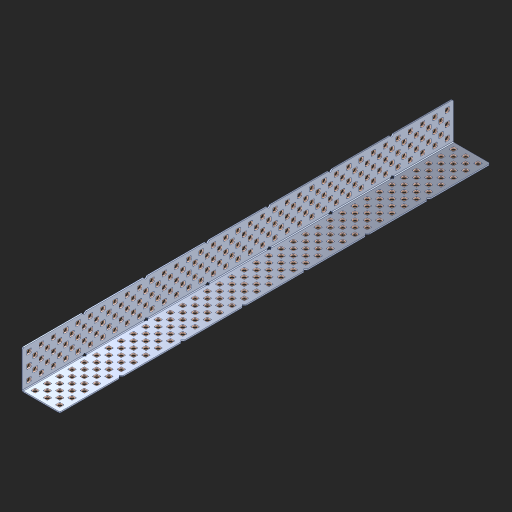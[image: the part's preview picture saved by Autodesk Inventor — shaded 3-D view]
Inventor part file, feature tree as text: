
AUTODESK INVENTOR PART (.ipt)
format: ipt  version: 2023 (Build 270158000, 158)  size: 3,318,784 bytes
history: native  units: in
note: dims shown in document units (in); Inventor stores cm internally (conversion verified against a paired STEP export)
features: other x388, extrude x344, sheet_metal_op x8, sketch x7, pattern_linear x3, mirror x1, chamfer x1
ambient origin geometry x8: Origin, YZ Plane, XZ Plane, XY Plane, X Axis, Y Axis, Z Axis, Center Point
bodies: Solid1 (feature_tree), Body (feature_tree)
feature tree (752):
  other  "Table"
  other  "Steel Angle 3x3x35"
  other  "Steel Angle 3x3x34"
  other  "Steel Angle 3x3x33"
  other  "Steel Angle 3x3x32"
  other  "Steel Angle 3x3x31"
  other  "Steel Angle 3x3x30"
  other  "Steel Angle 3x3x29"
  other  "Steel Angle 3x3x28"
  other  "Steel Angle 3x3x27"
  other  "Steel Angle 3x3x26"
  other  "Steel Angle 3x3x25"
  other  "Steel Angle 3x3x24"
  other  "Steel Angle 3x3x23"
  other  "Steel Angle 3x3x22"
  other  "Steel Angle 3x3x21"
  other  "Steel Angle 3x3x20"
  other  "Steel Angle 3x3x19"
  other  "Steel Angle 3x3x18"
  other  "Steel Angle 3x3x17"
  other  "Steel Angle 3x3x16"
  other  "Steel Angle 3x3x15"
  other  "Steel Angle 3x3x14"
  other  "Steel Angle 3x3x13"
  other  "Steel Angle 3x3x12"
  other  "Steel Angle 3x3x11"
  other  "Steel Angle 3x3x10"
  other  "Steel Angle 3x3x9"
  other  "Steel Angle 3x3x8"
  other  "Steel Angle 3x3x7"
  other  "Steel Angle 3x3x6"
  other  "Steel Angle 3x3x5"
  other  "Steel Angle 3x3x4"
  other  "Steel Angle 3x3x3"
  other  "Steel Angle 3x3x2"
  other  "Steel Angle 3x3x1"
  sheet_metal_op  "Flanges"
  sheet_metal_op  "Body Pattern"
  pattern_linear  "Center Double"  Spacing1=1.5in  [1 undecoded]
  pattern_linear  "Center Pattern"  Spacing1=0.1875in  [1 undecoded]
  other  "Arc Length"
  pattern_linear  "Notch Pattern"  Spacing1=0.0469in  [1 undecoded]
  other  "Diagonal Plane"
  mirror  "Everything Mirrored"
  chamfer  "End Chamfer"
  sketch  "Sketch1"  dims[d0=1.5in]
  other  "Plate1"
  sketch  "Sketch2"  dims[d1=17.5in]
  other  "Plate2"
  sheet_metal_op  "Bend1"
  sheet_metal_op  "Corner1"
  sketch  "Sketch8"  dims[d2=0.0469in]
  sketch  "Sketch9"  dims[d3=0.0469in]
  other  "Srf91"
  sheet_metal_op  "Body Pattern Sketch"
  other  "Srf92"
  sketch  "Sketch13"  dims[d4=0.0234in]
  sketch  "Sketch15"  dims[d5=0.0938in]
  sketch  "Sketch16"  dims[d6=0.0469in d7=1.5in d8=90.0deg d9=0.0312in d10=0.1875in d11=0.0469in d12=0.0469in d49=0.182in d50=0.02in d52=0.25in d53=0.0469in d54=0.0in d55=0.172in d56=1.0in d57=0.0in d85=0.1473in d86=0.1659in d89=0.0469in d90=0.0in d91=0.04in d92=0.0491in d95=2.5in d96=0.04in d97=0.25in d98=45.0deg d106=0.182in d107=0.02in d110=0.0469in d111=0.0in d112=0.172in d113=0.5in d114=0.0in d117=0.5in d126=0.0491in d127=0.1227in d128=0.08in d129=0.04in d130=2.5in d131=0.25in d132=13.7795in d134=0.5in d135=1.1811in d137=0.5in d140=0.5in d141=1.0in d142=0.3937in d144=0.5in d145=0.071in d146=0.7874in d148=0.5in]
  other  "Srf786"
  other  "Srf856"
  other  "Srf889"
  other  "Srf890"
  other  "Srf891"
  other  "Srf1275"
  other  "Srf1276"
  other  "Srf1278"
  other  "Srf1277"
  other  "Srf1285"
  other  "Srf1286"
  other  "Srf1287"
  other  "Srf1445"
  other  "Srf1446"
  other  "Srf1447"
  other  "Srf1448"
  other  "Srf1449"
  other  "Srf1537"
  other  "Srf1538"
  other  "Srf1539"
  other  "Srf1540"
  other  "Srf1541"
  other  "Srf1807"
  other  "Srf1808"
  other  "Srf1809"
  other  "Srf1810"
  other  "Srf1811"
  other  "Srf1812"
  other  "Srf1813"
  other  "Srf1814"
  other  "Srf1815"
  other  "Srf1816"
  other  "Srf1817"
  other  "Srf1818"
  other  "Srf1819"
  other  "Srf1820"
  other  "Srf1821"
  other  "Srf1822"
  other  "Srf1823"
  other  "Srf1824"
  other  "Srf1825"
  other  "Srf1826"
  other  "Srf1827"
  other  "Srf1828"
  other  "Srf1829"
  other  "Srf1830"
  other  "Srf1831"
  other  "Srf1959"
  other  "Srf1960"
  other  "Srf1961"
  other  "Srf1962"
  other  "Srf1963"
  other  "Srf1964"
  other  "Srf1965"
  other  "Srf1966"
  other  "Srf1967"
  other  "Srf1968"
  other  "Srf1969"
  other  "Srf1970"
  other  "Srf1971"
  other  "Srf1972"
  other  "Srf1973"
  other  "Srf1974"
  other  "Srf1975"
  other  "Srf1976"
  other  "Srf1977"
  other  "Srf1978"
  other  "Srf1979"
  other  "Srf1980"
  other  "Srf1981"
  other  "Srf1982"
  other  "Srf1983"
  other  "Srf2009"
  other  "Srf2010"
  other  "Srf2011"
  other  "Srf2012"
  other  "Srf2013"
  other  "Srf2014"
  other  "Srf2015"
  other  "Srf2016"
  other  "Srf2017"
  other  "Srf2018"
  other  "Srf2019"
  other  "Srf2020"
  other  "Srf2021"
  other  "Srf2022"
  other  "Srf2023"
  other  "Srf2024"
  other  "Srf2025"
  other  "Srf2026"
  other  "Srf2027"
  other  "Srf2028"
  other  "Srf2029"
  other  "Srf2030"
  other  "Srf2031"
  other  "Srf2032"
  other  "Srf2033"
  other  "Srf2034"
  other  "Srf2035"
  other  "Srf2036"
  other  "Srf2037"
  other  "Srf2038"
  other  "Srf2039"
  other  "Srf2040"
  other  "Srf2041"
  other  "Srf2042"
  other  "Srf2043"
  other  "Srf2044"
  other  "Srf2045"
  other  "Srf2046"
  other  "Srf2047"
  other  "Srf2048"
  other  "Srf2049"
  other  "Srf2050"
  other  "Srf2051"
  other  "Srf2052"
  other  "Srf2053"
  other  "Srf2054"
  other  "Srf2055"
  other  "Srf2056"
  other  "Srf2057"
  other  "Srf2058"
  other  "Srf2059"
  other  "Srf2060"
  other  "Srf2061"
  other  "Srf2062"
  other  "Srf2063"
  other  "Srf2064"
  other  "Srf2065"
  other  "Srf2066"
  other  "Srf2067"
  other  "Srf2068"
  other  "Srf2069"
  other  "Srf2070"
  other  "Srf2071"
  other  "Srf2072"
  other  "Srf2073"
  other  "Srf2074"
  other  "Srf2075"
  other  "Srf2076"
  other  "Srf2077"
  other  "Srf2078"
  other  "Srf2079"
  other  "Srf2080"
  other  "Srf2081"
  other  "Srf2082"
  other  "Srf2083"
  other  "Srf2084"
  other  "Srf2085"
  other  "Srf2086"
  other  "Srf2087"
  other  "Srf2088"
  other  "Srf2089"
  other  "Srf2090"
  other  "Srf2091"
  other  "Srf2092"
  other  "Srf2093"
  other  "Srf2094"
  other  "Srf2095"
  other  "Srf2096"
  other  "Srf2097"
  other  "Srf2098"
  other  "Srf2099"
  other  "Srf2100"
  other  "Srf2101"
  other  "Srf2102"
  other  "Srf2103"
  other  "Srf2104"
  other  "Srf2105"
  other  "Srf2106"
  other  "Srf2107"
  other  "Srf2108"
  other  "Srf2109"
  other  "Srf2110"
  other  "Srf2111"
  other  "Srf2112"
  other  "Srf2113"
  other  "Srf2114"
  other  "Srf2115"
  other  "Srf2116"
  other  "Srf2117"
  other  "Srf2118"
  other  "Srf2119"
  other  "Srf2120"
  other  "Srf2121"
  other  "Srf2122"
  other  "Srf2123"
  other  "Srf2124"
  other  "Srf2125"
  other  "Srf2126"
  other  "Srf2127"
  other  "Srf2128"
  other  "Srf2129"
  other  "Srf2130"
  other  "Srf2131"
  other  "Srf2132"
  other  "Srf2133"
  other  "Srf2134"
  other  "Srf2135"
  other  "Srf2136"
  other  "Srf2137"
  other  "Srf2138"
  other  "Srf2139"
  other  "Srf2140"
  other  "Srf2141"
  other  "Srf2142"
  other  "Srf2143"
  other  "Srf2144"
  other  "Srf2145"
  other  "Srf2146"
  other  "Srf2147"
  other  "Srf2148"
  other  "Srf2149"
  other  "Srf2150"
  other  "Srf2151"
  other  "Srf2152"
  other  "Srf2153"
  other  "Srf2154"
  other  "Srf2155"
  other  "Srf2156"
  other  "Srf2157"
  other  "Srf2158"
  other  "Srf2159"
  other  "Srf2160"
  other  "Srf2161"
  other  "Srf2162"
  other  "Srf2163"
  other  "Srf2164"
  other  "Srf2165"
  other  "Srf2166"
  other  "Srf2167"
  other  "Srf2168"
  other  "Srf2169"
  other  "Srf2170"
  other  "Srf2171"
  other  "Srf2172"
  other  "Srf2173"
  other  "Srf2174"
  other  "Srf2175"
  other  "Srf2176"
  other  "Srf2177"
  other  "Srf2178"
  other  "Srf2179"
  other  "Srf2180"
  other  "Srf2181"
  other  "Srf2182"
  other  "Srf2183"
  other  "Srf2184"
  other  "Srf2185"
  other  "Srf2186"
  other  "Srf2187"
  other  "Srf2188"
  other  "Srf2189"
  other  "Srf2190"
  other  "Srf2191"
  other  "Srf2192"
  other  "Srf2193"
  other  "Srf2194"
  other  "Srf2195"
  other  "Srf2196"
  other  "Srf2197"
  other  "Srf2198"
  other  "Srf2199"
  other  "Srf2200"
  other  "Srf2201"
  other  "Srf2202"
  other  "Srf2203"
  other  "Srf2204"
  other  "Srf2205"
  other  "Srf2206"
  other  "Srf2207"
  other  "Srf2208"
  other  "Srf2209"
  other  "Srf2210"
  other  "Srf2211"
  other  "Srf2212"
  other  "Srf2213"
  other  "Srf2214"
  other  "Srf2215"
  other  "Srf2216"
  other  "Srf2217"
  other  "Srf2218"
  other  "Srf2219"
  other  "Srf2220"
  other  "Srf2221"
  other  "Srf2222"
  other  "Srf2223"
  other  "Srf2224"
  other  "Srf2225"
  other  "Srf2226"
  other  "Srf2227"
  other  "Srf2228"
  other  "Srf2229"
  other  "Srf2230"
  other  "Srf2231"
  other  "Srf2232"
  other  "Srf2233"
  other  "Srf2234"
  other  "Srf2235"
  other  "Srf2236"
  other  "Srf2237"
  other  "Srf2238"
  other  "Srf2239"
  other  "Srf2240"
  other  "Srf2241"
  other  "Srf2242"
  other  "Srf2243"
  other  "Srf2244"
  other  "Srf2245"
  other  "Srf2246"
  other  "Srf2247"
  other  "Srf2248"
  other  "Srf2249"
  other  "Srf2250"
  other  "Srf2251"
  other  "Srf2252"
  other  "Srf2253"
  other  "Srf2254"
  other  "Srf2255"
  other  "Srf2256"
  other  "Srf2257"
  other  "Srf2258"
  other  "Srf2259"
  other  "Srf2260"
  other  "Srf2261"
  other  "Srf2262"
  other  "Srf2263"
  other  "Srf2264"
  other  "Srf2265"
  other  "Srf2266"
  other  "Srf2267"
  other  "Srf2268"
  other  "Srf2269"
  other  "Srf2270"
  other  "Srf2271"
  other  "Srf2272"
  other  "Srf2273"
  other  "Srf2274"
  other  "Srf2275"
  other  "Srf2276"
  other  "Srf2277"
  other  "Srf2278"
  other  "Srf2279"
  other  "Srf2280"
  sheet_metal_op  "Body Stamp"
  sheet_metal_op  "Body Circle"
  other  "Center Stamp"
  other  "Center Circle"
  sheet_metal_op  "Notch"
  extrude  "ExtrusionSrf92"  Depth=0.0469in
  extrude  "ExtrusionSrf856"  Depth=0.3937in
  extrude  "ExtrusionSrf889"  Depth=0.02in
  extrude  "ExtrusionSrf890"  Depth=0.25in
  extrude  "ExtrusionSrf891"  Depth=0.0469in
  extrude  "ExtrusionSrf1275"  TaperAngle=0.0deg  [1 undecoded]
  extrude  "ExtrusionSrf1276"  Depth=0.3937in
  extrude  "ExtrusionSrf1277"  Depth=0.3937in TaperAngle=0.0deg
  extrude  "ExtrusionSrf1345"  Depth=0.3937in
  extrude  "ExtrusionSrf1346"  Depth=0.3937in
  extrude  "ExtrusionSrf1347"  Depth=0.0469in
  extrude  "ExtrusionSrf1348"  Depth=0.3937in TaperAngle=0.0deg
  extrude  "ExtrusionSrf1445"  Depth=0.3937in
  extrude  "ExtrusionSrf1446"  Depth=0.25in TaperAngle=45.0deg
  extrude  "ExtrusionSrf1447"  Depth=0.3937in
  extrude  "ExtrusionSrf1448"  Depth=0.02in
  extrude  "ExtrusionSrf1449"  Depth=0.0469in
  extrude  "ExtrusionSrf1537"  TaperAngle=0.0deg  [1 undecoded]
  extrude  "ExtrusionSrf1538"  Depth=0.3937in
  extrude  "ExtrusionSrf1539"  Depth=0.3937in TaperAngle=0.0deg
  extrude  "ExtrusionSrf1540"  Depth=0.3937in
  extrude  "ExtrusionSrf1541"  Depth=0.3937in
  extrude  "ExtrusionSrf1807"  Depth=0.3937in
  extrude  "ExtrusionSrf1808"  Depth=0.3937in
  extrude  "ExtrusionSrf1809"  Depth=0.3937in
  extrude  "ExtrusionSrf1810"  Depth=0.3937in
  extrude  "ExtrusionSrf1811"  Depth=0.25in
  extrude  "ExtrusionSrf1812"  Depth=0.3937in
  extrude  "ExtrusionSrf1813"  Depth=0.3937in
  extrude  "ExtrusionSrf1814"  Depth=0.3937in
  extrude  "ExtrusionSrf1815"  Depth=0.3937in
  extrude  "ExtrusionSrf1816"  Depth=0.3937in
  extrude  "ExtrusionSrf1817"  Depth=0.3937in
  extrude  "ExtrusionSrf1818"  Depth=0.3937in
  extrude  "ExtrusionSrf1819"  [1 undecoded]
  extrude  "ExtrusionSrf1820"  [1 undecoded]
  extrude  "ExtrusionSrf1821"  [1 undecoded]
  extrude  "ExtrusionSrf1822"  [1 undecoded]
  extrude  "ExtrusionSrf1823"  [1 undecoded]
  extrude  "ExtrusionSrf1824"  [1 undecoded]
  extrude  "ExtrusionSrf1825"  [1 undecoded]
  extrude  "ExtrusionSrf1826"  [1 undecoded]
  extrude  "ExtrusionSrf1827"  [1 undecoded]
  extrude  "ExtrusionSrf1828"  [1 undecoded]
  extrude  "ExtrusionSrf1829"  [1 undecoded]
  extrude  "ExtrusionSrf1830"  [1 undecoded]
  extrude  "ExtrusionSrf1831"  [1 undecoded]
  extrude  "ExtrusionSrf1959"  [1 undecoded]
  extrude  "ExtrusionSrf1960"  [1 undecoded]
  extrude  "ExtrusionSrf1961"  [1 undecoded]
  extrude  "ExtrusionSrf1962"  [1 undecoded]
  extrude  "ExtrusionSrf1963"  [1 undecoded]
  extrude  "ExtrusionSrf1964"  [1 undecoded]
  extrude  "ExtrusionSrf1965"  [1 undecoded]
  extrude  "ExtrusionSrf1966"  [1 undecoded]
  extrude  "ExtrusionSrf1967"  [1 undecoded]
  extrude  "ExtrusionSrf1968"  [1 undecoded]
  extrude  "ExtrusionSrf1969"  [1 undecoded]
  extrude  "ExtrusionSrf1970"  [1 undecoded]
  extrude  "ExtrusionSrf1971"  [1 undecoded]
  extrude  "ExtrusionSrf1972"  [1 undecoded]
  extrude  "ExtrusionSrf1973"  [1 undecoded]
  extrude  "ExtrusionSrf1974"  [1 undecoded]
  extrude  "ExtrusionSrf1975"  [1 undecoded]
  extrude  "ExtrusionSrf1976"  [1 undecoded]
  extrude  "ExtrusionSrf1977"  [1 undecoded]
  extrude  "ExtrusionSrf1978"  [1 undecoded]
  extrude  "ExtrusionSrf1979"  [1 undecoded]
  extrude  "ExtrusionSrf1980"  [1 undecoded]
  extrude  "ExtrusionSrf1981"  [1 undecoded]
  extrude  "ExtrusionSrf1982"  [1 undecoded]
  extrude  "ExtrusionSrf1983"  [1 undecoded]
  extrude  "ExtrusionSrf2009"  [1 undecoded]
  extrude  "ExtrusionSrf2010"  [1 undecoded]
  extrude  "ExtrusionSrf2011"  [1 undecoded]
  extrude  "ExtrusionSrf2012"  [1 undecoded]
  extrude  "ExtrusionSrf2013"  [1 undecoded]
  extrude  "ExtrusionSrf2014"  [1 undecoded]
  extrude  "ExtrusionSrf2015"  [1 undecoded]
  extrude  "ExtrusionSrf2016"  [1 undecoded]
  extrude  "ExtrusionSrf2017"  [1 undecoded]
  extrude  "ExtrusionSrf2018"  [1 undecoded]
  extrude  "ExtrusionSrf2019"  [1 undecoded]
  extrude  "ExtrusionSrf2020"  [1 undecoded]
  extrude  "ExtrusionSrf2021"  [1 undecoded]
  extrude  "ExtrusionSrf2022"  [1 undecoded]
  extrude  "ExtrusionSrf2023"  [1 undecoded]
  extrude  "ExtrusionSrf2024"  [1 undecoded]
  extrude  "ExtrusionSrf2025"  [1 undecoded]
  extrude  "ExtrusionSrf2026"  [1 undecoded]
  extrude  "ExtrusionSrf2027"  [1 undecoded]
  extrude  "ExtrusionSrf2028"  [1 undecoded]
  extrude  "ExtrusionSrf2029"  [1 undecoded]
  extrude  "ExtrusionSrf2030"  [1 undecoded]
  extrude  "ExtrusionSrf2031"  [1 undecoded]
  extrude  "ExtrusionSrf2032"  [1 undecoded]
  extrude  "ExtrusionSrf2033"  [1 undecoded]
  extrude  "ExtrusionSrf2034"  [1 undecoded]
  extrude  "ExtrusionSrf2035"  [1 undecoded]
  extrude  "ExtrusionSrf2036"  [1 undecoded]
  extrude  "ExtrusionSrf2037"  [1 undecoded]
  extrude  "ExtrusionSrf2038"  [1 undecoded]
  extrude  "ExtrusionSrf2039"  [1 undecoded]
  extrude  "ExtrusionSrf2040"  [1 undecoded]
  extrude  "ExtrusionSrf2041"  [1 undecoded]
  extrude  "ExtrusionSrf2042"  [1 undecoded]
  extrude  "ExtrusionSrf2043"  [1 undecoded]
  extrude  "ExtrusionSrf2044"  [1 undecoded]
  extrude  "ExtrusionSrf2045"  [1 undecoded]
  extrude  "ExtrusionSrf2046"  [1 undecoded]
  extrude  "ExtrusionSrf2047"  [1 undecoded]
  extrude  "ExtrusionSrf2048"  [1 undecoded]
  extrude  "ExtrusionSrf2049"  [1 undecoded]
  extrude  "ExtrusionSrf2050"  [1 undecoded]
  extrude  "ExtrusionSrf2051"  [1 undecoded]
  extrude  "ExtrusionSrf2052"  [1 undecoded]
  extrude  "ExtrusionSrf2053"  [1 undecoded]
  extrude  "ExtrusionSrf2054"  [1 undecoded]
  extrude  "ExtrusionSrf2055"  [1 undecoded]
  extrude  "ExtrusionSrf2056"  [1 undecoded]
  extrude  "ExtrusionSrf2057"  [1 undecoded]
  extrude  "ExtrusionSrf2058"  [1 undecoded]
  extrude  "ExtrusionSrf2059"  [1 undecoded]
  extrude  "ExtrusionSrf2060"  [1 undecoded]
  extrude  "ExtrusionSrf2061"  [1 undecoded]
  extrude  "ExtrusionSrf2062"  [1 undecoded]
  extrude  "ExtrusionSrf2063"  [1 undecoded]
  extrude  "ExtrusionSrf2064"  [1 undecoded]
  extrude  "ExtrusionSrf2065"  [1 undecoded]
  extrude  "ExtrusionSrf2066"  [1 undecoded]
  extrude  "ExtrusionSrf2067"  [1 undecoded]
  extrude  "ExtrusionSrf2068"  [1 undecoded]
  extrude  "ExtrusionSrf2069"  [1 undecoded]
  extrude  "ExtrusionSrf2070"  [1 undecoded]
  extrude  "ExtrusionSrf2071"  [1 undecoded]
  extrude  "ExtrusionSrf2072"  [1 undecoded]
  extrude  "ExtrusionSrf2073"  [1 undecoded]
  extrude  "ExtrusionSrf2074"  [1 undecoded]
  extrude  "ExtrusionSrf2075"  [1 undecoded]
  extrude  "ExtrusionSrf2076"  [1 undecoded]
  extrude  "ExtrusionSrf2077"  [1 undecoded]
  extrude  "ExtrusionSrf2078"  [1 undecoded]
  extrude  "ExtrusionSrf2079"  [1 undecoded]
  extrude  "ExtrusionSrf2080"  [1 undecoded]
  extrude  "ExtrusionSrf2081"  [1 undecoded]
  extrude  "ExtrusionSrf2082"  [1 undecoded]
  extrude  "ExtrusionSrf2083"  [1 undecoded]
  extrude  "ExtrusionSrf2084"  [1 undecoded]
  extrude  "ExtrusionSrf2085"  [1 undecoded]
  extrude  "ExtrusionSrf2086"  [1 undecoded]
  extrude  "ExtrusionSrf2087"  [1 undecoded]
  extrude  "ExtrusionSrf2088"  [1 undecoded]
  extrude  "ExtrusionSrf2089"  [1 undecoded]
  extrude  "ExtrusionSrf2090"  [1 undecoded]
  extrude  "ExtrusionSrf2091"  [1 undecoded]
  extrude  "ExtrusionSrf2092"  [1 undecoded]
  extrude  "ExtrusionSrf2093"  [1 undecoded]
  extrude  "ExtrusionSrf2094"  [1 undecoded]
  extrude  "ExtrusionSrf2095"  [1 undecoded]
  extrude  "ExtrusionSrf2096"  [1 undecoded]
  extrude  "ExtrusionSrf2097"  [1 undecoded]
  extrude  "ExtrusionSrf2098"  [1 undecoded]
  extrude  "ExtrusionSrf2099"  [1 undecoded]
  extrude  "ExtrusionSrf2100"  [1 undecoded]
  extrude  "ExtrusionSrf2101"  [1 undecoded]
  extrude  "ExtrusionSrf2102"  [1 undecoded]
  extrude  "ExtrusionSrf2103"  [1 undecoded]
  extrude  "ExtrusionSrf2104"  [1 undecoded]
  extrude  "ExtrusionSrf2105"  [1 undecoded]
  extrude  "ExtrusionSrf2106"  [1 undecoded]
  extrude  "ExtrusionSrf2107"  [1 undecoded]
  extrude  "ExtrusionSrf2108"  [1 undecoded]
  extrude  "ExtrusionSrf2109"  [1 undecoded]
  extrude  "ExtrusionSrf2110"  [1 undecoded]
  extrude  "ExtrusionSrf2111"  [1 undecoded]
  extrude  "ExtrusionSrf2112"  [1 undecoded]
  extrude  "ExtrusionSrf2113"  [1 undecoded]
  extrude  "ExtrusionSrf2114"  [1 undecoded]
  extrude  "ExtrusionSrf2115"  [1 undecoded]
  extrude  "ExtrusionSrf2116"  [1 undecoded]
  extrude  "ExtrusionSrf2117"  [1 undecoded]
  extrude  "ExtrusionSrf2118"  [1 undecoded]
  extrude  "ExtrusionSrf2119"  [1 undecoded]
  extrude  "ExtrusionSrf2120"  [1 undecoded]
  extrude  "ExtrusionSrf2121"  [1 undecoded]
  extrude  "ExtrusionSrf2122"  [1 undecoded]
  extrude  "ExtrusionSrf2123"  [1 undecoded]
  extrude  "ExtrusionSrf2124"  [1 undecoded]
  extrude  "ExtrusionSrf2125"  [1 undecoded]
  extrude  "ExtrusionSrf2126"  [1 undecoded]
  extrude  "ExtrusionSrf2127"  [1 undecoded]
  extrude  "ExtrusionSrf2128"  [1 undecoded]
  extrude  "ExtrusionSrf2129"  [1 undecoded]
  extrude  "ExtrusionSrf2130"  [1 undecoded]
  extrude  "ExtrusionSrf2131"  [1 undecoded]
  extrude  "ExtrusionSrf2132"  [1 undecoded]
  extrude  "ExtrusionSrf2133"  [1 undecoded]
  extrude  "ExtrusionSrf2134"  [1 undecoded]
  extrude  "ExtrusionSrf2135"  [1 undecoded]
  extrude  "ExtrusionSrf2136"  [1 undecoded]
  extrude  "ExtrusionSrf2137"  [1 undecoded]
  extrude  "ExtrusionSrf2138"  [1 undecoded]
  extrude  "ExtrusionSrf2139"  [1 undecoded]
  extrude  "ExtrusionSrf2140"  [1 undecoded]
  extrude  "ExtrusionSrf2141"  [1 undecoded]
  extrude  "ExtrusionSrf2142"  [1 undecoded]
  extrude  "ExtrusionSrf2143"  [1 undecoded]
  extrude  "ExtrusionSrf2144"  [1 undecoded]
  extrude  "ExtrusionSrf2145"  [1 undecoded]
  extrude  "ExtrusionSrf2146"  [1 undecoded]
  extrude  "ExtrusionSrf2147"  [1 undecoded]
  extrude  "ExtrusionSrf2148"  [1 undecoded]
  extrude  "ExtrusionSrf2149"  [1 undecoded]
  extrude  "ExtrusionSrf2150"  [1 undecoded]
  extrude  "ExtrusionSrf2151"  [1 undecoded]
  extrude  "ExtrusionSrf2152"  [1 undecoded]
  extrude  "ExtrusionSrf2153"  [1 undecoded]
  extrude  "ExtrusionSrf2154"  [1 undecoded]
  extrude  "ExtrusionSrf2155"  [1 undecoded]
  extrude  "ExtrusionSrf2156"  [1 undecoded]
  extrude  "ExtrusionSrf2157"  [1 undecoded]
  extrude  "ExtrusionSrf2158"  [1 undecoded]
  extrude  "ExtrusionSrf2159"  [1 undecoded]
  extrude  "ExtrusionSrf2160"  [1 undecoded]
  extrude  "ExtrusionSrf2161"  [1 undecoded]
  extrude  "ExtrusionSrf2162"  [1 undecoded]
  extrude  "ExtrusionSrf2163"  [1 undecoded]
  extrude  "ExtrusionSrf2164"  [1 undecoded]
  extrude  "ExtrusionSrf2165"  [1 undecoded]
  extrude  "ExtrusionSrf2166"  [1 undecoded]
  extrude  "ExtrusionSrf2167"  [1 undecoded]
  extrude  "ExtrusionSrf2168"  [1 undecoded]
  extrude  "ExtrusionSrf2169"  [1 undecoded]
  extrude  "ExtrusionSrf2170"  [1 undecoded]
  extrude  "ExtrusionSrf2171"  [1 undecoded]
  extrude  "ExtrusionSrf2172"  [1 undecoded]
  extrude  "ExtrusionSrf2173"  [1 undecoded]
  extrude  "ExtrusionSrf2174"  [1 undecoded]
  extrude  "ExtrusionSrf2175"  [1 undecoded]
  extrude  "ExtrusionSrf2176"  [1 undecoded]
  extrude  "ExtrusionSrf2177"  [1 undecoded]
  extrude  "ExtrusionSrf2178"  [1 undecoded]
  extrude  "ExtrusionSrf2179"  [1 undecoded]
  extrude  "ExtrusionSrf2180"  [1 undecoded]
  extrude  "ExtrusionSrf2181"  [1 undecoded]
  extrude  "ExtrusionSrf2182"  [1 undecoded]
  extrude  "ExtrusionSrf2183"  [1 undecoded]
  extrude  "ExtrusionSrf2184"  [1 undecoded]
  extrude  "ExtrusionSrf2185"  [1 undecoded]
  extrude  "ExtrusionSrf2186"  [1 undecoded]
  extrude  "ExtrusionSrf2187"  [1 undecoded]
  extrude  "ExtrusionSrf2188"  [1 undecoded]
  extrude  "ExtrusionSrf2189"  [1 undecoded]
  extrude  "ExtrusionSrf2190"  [1 undecoded]
  extrude  "ExtrusionSrf2191"  [1 undecoded]
  extrude  "ExtrusionSrf2192"  [1 undecoded]
  extrude  "ExtrusionSrf2193"  [1 undecoded]
  extrude  "ExtrusionSrf2194"  [1 undecoded]
  extrude  "ExtrusionSrf2195"  [1 undecoded]
  extrude  "ExtrusionSrf2196"  [1 undecoded]
  extrude  "ExtrusionSrf2197"  [1 undecoded]
  extrude  "ExtrusionSrf2198"  [1 undecoded]
  extrude  "ExtrusionSrf2199"  [1 undecoded]
  extrude  "ExtrusionSrf2200"  [1 undecoded]
  extrude  "ExtrusionSrf2201"  [1 undecoded]
  extrude  "ExtrusionSrf2202"  [1 undecoded]
  extrude  "ExtrusionSrf2203"  [1 undecoded]
  extrude  "ExtrusionSrf2204"  [1 undecoded]
  extrude  "ExtrusionSrf2205"  [1 undecoded]
  extrude  "ExtrusionSrf2206"  [1 undecoded]
  extrude  "ExtrusionSrf2207"  [1 undecoded]
  extrude  "ExtrusionSrf2208"  [1 undecoded]
  extrude  "ExtrusionSrf2209"  [1 undecoded]
  extrude  "ExtrusionSrf2210"  [1 undecoded]
  extrude  "ExtrusionSrf2211"  [1 undecoded]
  extrude  "ExtrusionSrf2212"  [1 undecoded]
  extrude  "ExtrusionSrf2213"  [1 undecoded]
  extrude  "ExtrusionSrf2214"  [1 undecoded]
  extrude  "ExtrusionSrf2215"  [1 undecoded]
  extrude  "ExtrusionSrf2216"  [1 undecoded]
  extrude  "ExtrusionSrf2217"  [1 undecoded]
  extrude  "ExtrusionSrf2218"  [1 undecoded]
  extrude  "ExtrusionSrf2219"  [1 undecoded]
  extrude  "ExtrusionSrf2220"  [1 undecoded]
  extrude  "ExtrusionSrf2221"  [1 undecoded]
  extrude  "ExtrusionSrf2222"  [1 undecoded]
  extrude  "ExtrusionSrf2223"  [1 undecoded]
  extrude  "ExtrusionSrf2224"  [1 undecoded]
  extrude  "ExtrusionSrf2225"  [1 undecoded]
  extrude  "ExtrusionSrf2226"  [1 undecoded]
  extrude  "ExtrusionSrf2227"  [1 undecoded]
  extrude  "ExtrusionSrf2228"  [1 undecoded]
  extrude  "ExtrusionSrf2229"  [1 undecoded]
  extrude  "ExtrusionSrf2230"  [1 undecoded]
  extrude  "ExtrusionSrf2231"  [1 undecoded]
  extrude  "ExtrusionSrf2232"  [1 undecoded]
  extrude  "ExtrusionSrf2233"  [1 undecoded]
  extrude  "ExtrusionSrf2234"  [1 undecoded]
  extrude  "ExtrusionSrf2235"  [1 undecoded]
  extrude  "ExtrusionSrf2236"  [1 undecoded]
  extrude  "ExtrusionSrf2237"  [1 undecoded]
  extrude  "ExtrusionSrf2238"  [1 undecoded]
  extrude  "ExtrusionSrf2239"  [1 undecoded]
  extrude  "ExtrusionSrf2240"  [1 undecoded]
  extrude  "ExtrusionSrf2241"  [1 undecoded]
  extrude  "ExtrusionSrf2242"  [1 undecoded]
  extrude  "ExtrusionSrf2243"  [1 undecoded]
  extrude  "ExtrusionSrf2244"  [1 undecoded]
  extrude  "ExtrusionSrf2245"  [1 undecoded]
  extrude  "ExtrusionSrf2246"  [1 undecoded]
  extrude  "ExtrusionSrf2247"  [1 undecoded]
  extrude  "ExtrusionSrf2248"  [1 undecoded]
  extrude  "ExtrusionSrf2249"  [1 undecoded]
  extrude  "ExtrusionSrf2250"  [1 undecoded]
  extrude  "ExtrusionSrf2251"  [1 undecoded]
  extrude  "ExtrusionSrf2252"  [1 undecoded]
  extrude  "ExtrusionSrf2253"  [1 undecoded]
  extrude  "ExtrusionSrf2254"  [1 undecoded]
  extrude  "ExtrusionSrf2255"  [1 undecoded]
  extrude  "ExtrusionSrf2256"  [1 undecoded]
  extrude  "ExtrusionSrf2257"  [1 undecoded]
  extrude  "ExtrusionSrf2258"  [1 undecoded]
  extrude  "ExtrusionSrf2259"  [1 undecoded]
  extrude  "ExtrusionSrf2260"  [1 undecoded]
  extrude  "ExtrusionSrf2261"  [1 undecoded]
  extrude  "ExtrusionSrf2262"  [1 undecoded]
  extrude  "ExtrusionSrf2263"  [1 undecoded]
  extrude  "ExtrusionSrf2264"  [1 undecoded]
  extrude  "ExtrusionSrf2265"  [1 undecoded]
  extrude  "ExtrusionSrf2266"  [1 undecoded]
  extrude  "ExtrusionSrf2267"  [1 undecoded]
  extrude  "ExtrusionSrf2268"  [1 undecoded]
  extrude  "ExtrusionSrf2269"  [1 undecoded]
  extrude  "ExtrusionSrf2270"  [1 undecoded]
  extrude  "ExtrusionSrf2271"  [1 undecoded]
  extrude  "ExtrusionSrf2272"  [1 undecoded]
  extrude  "ExtrusionSrf2273"  [1 undecoded]
  extrude  "ExtrusionSrf2274"  [1 undecoded]
  extrude  "ExtrusionSrf2275"  [1 undecoded]
  extrude  "ExtrusionSrf2276"  [1 undecoded]
  extrude  "ExtrusionSrf2277"  [1 undecoded]
  extrude  "ExtrusionSrf2278"  [1 undecoded]
  extrude  "ExtrusionSrf2279"  [1 undecoded]
  extrude  "ExtrusionSrf2280"  [1 undecoded]
note: 315 required parameter values undecoded (feature->parameter linkage not recoverable at this tier; creation-order binding heuristic only, values carry confidence <= 0.55)
